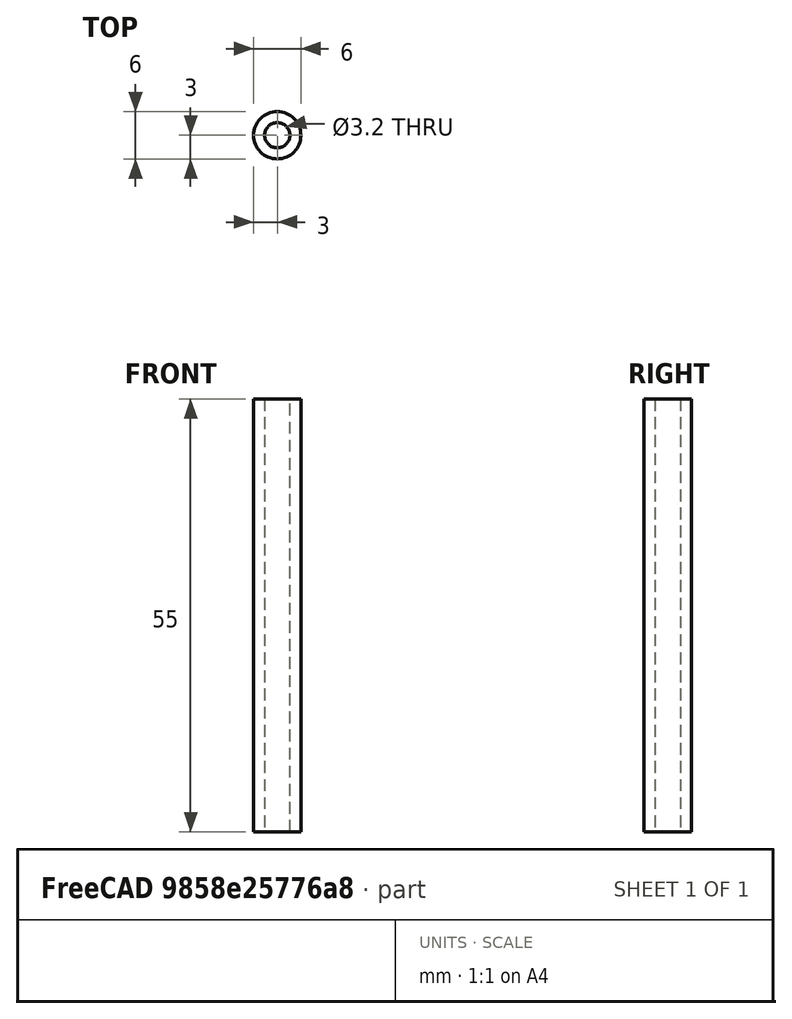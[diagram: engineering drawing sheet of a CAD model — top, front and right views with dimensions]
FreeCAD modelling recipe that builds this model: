
FCSTD DOCUMENT  (FreeCAD 1.0R39109 (Git))
Label: 55mm_spacer
License: All rights reserved
LicenseURL: https://en.wikipedia.org/wiki/All_rights_reserved
objects: Sketcher::SketchObject×1, PartDesign::Pad×1, PartDesign::Body×1
note: 6 computed .brp shape members not serialized (recipe doc carries the construction recipe); baked Part::Feature solids carry a one-line shape summary decoded from their .brp

FEATURE [Sketcher::SketchObject] Sketch
  ArcFitTolerance = 1e-06
  AttachmentSupport = -> [XY_Plane]
  FullyConstrained = true
  MakeInternals = false
  MapMode = 5
  sketch-geometry (2):
    g0: Circle CenterX=0 CenterY=0 CenterZ=0 NormalX=0 NormalY=0 NormalZ=1 AngleXU=0 Radius=1.6
    g1: Circle CenterX=0 CenterY=0 CenterZ=0 NormalX=0 NormalY=0 NormalZ=1 AngleXU=0 Radius=3
  constraints (4):
    c: Coincident(g0,g-1)
    c: Coincident(g1,g0)
    c: Diameter(g0) = 3.2
    c: Diameter(g1) = 6
FEATURE [PartDesign::Pad] Pad
  Direction = (0,0,1)
  Length = 55
  Length2 = 10
  Profile = -> Sketch
  ReferenceAxis = -> Sketch [N_Axis]
  Refine = true
  Suppressed = false
  Type = 0
FEATURE [PartDesign::Body] Body
  AllowCompound = false
  Group = -> [Sketch,Pad]
  Origin = -> Origin
  Tip = -> Pad
